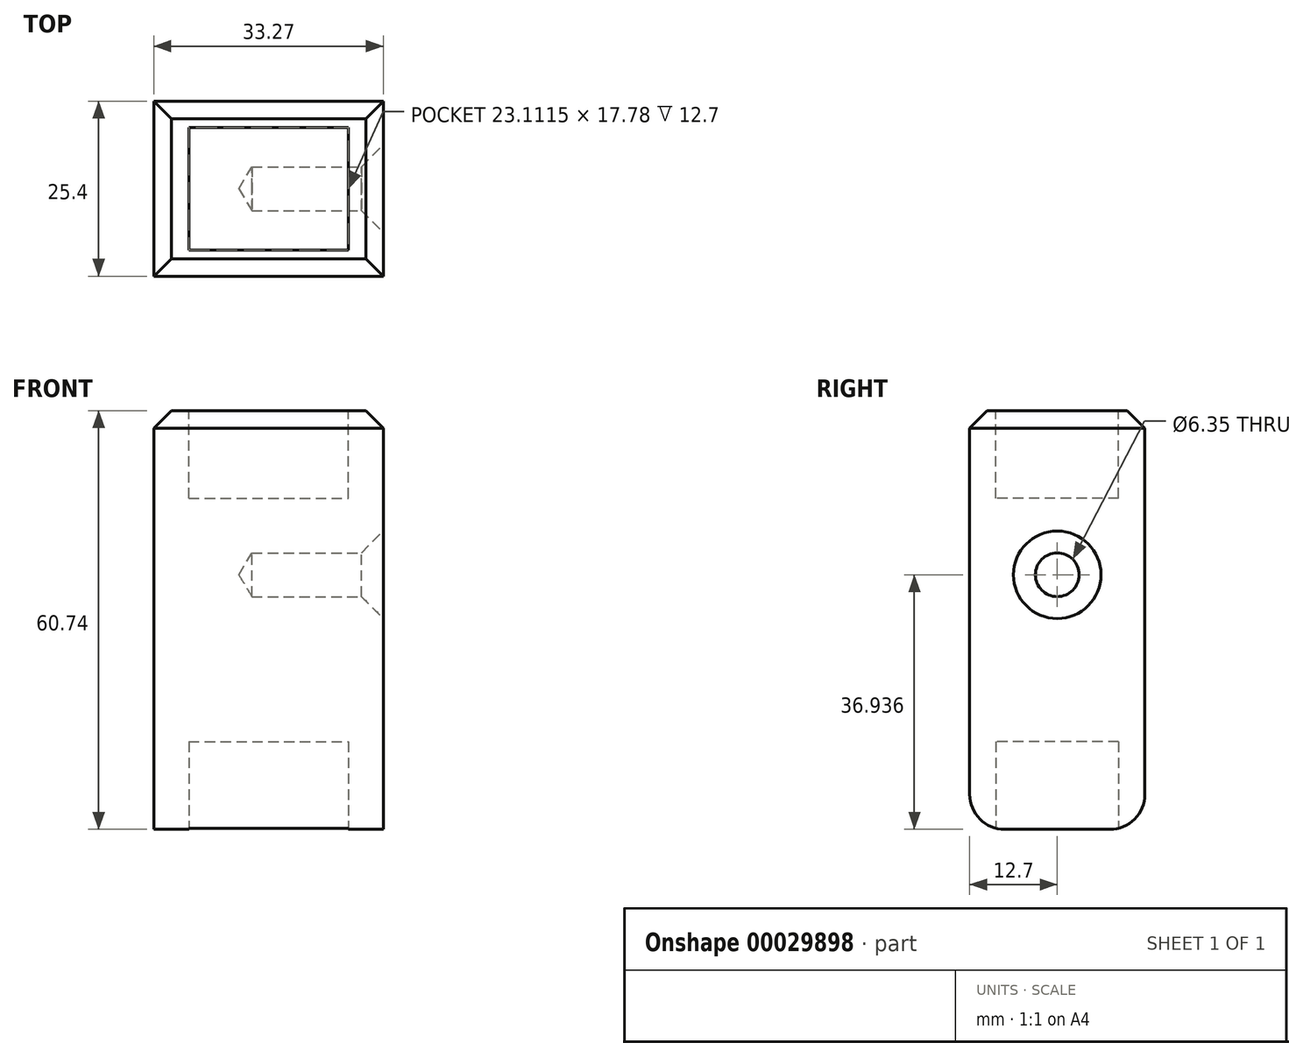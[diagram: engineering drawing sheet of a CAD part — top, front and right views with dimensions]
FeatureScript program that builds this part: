
annotation { "Feature Type Name" : "Feature", "Feature Type Description" : "" }
export const myFeature = defineFeature(function(context is Context, id is Id, definition is map)
    precondition{}
    {
        {
            var Q0;
            Q0=qCreatedBy(makeId("Front.planeOp"),FACE);
            var sketch = newSketch(context, id + "F0", { "sketchPlane" : qUnion([Q0])});
            skLineSegment(sketch, "E0", {"start": v(0, 0) * mm, "end": v(0, 30.37) * mm});
            skLineSegment(sketch, "E1", {"start": v(0, 30.37) * mm, "end": v(33.27, 30.37) * mm});
            skLineSegment(sketch, "E2", {"start": v(33.27, 30.37) * mm, "end": v(33.27, 0) * mm});
            skLineSegment(sketch, "E3", {"start": v(33.27, 0) * mm, "end": v(0, 0) * mm});
            skSolve(sketch);
        }
        {
            var Q0;
            Q0=makeQuery(id+"F0.imprint","IMPRINT",FACE,{"disambiguationData":[TD([[makeQuery(id+"F0.imprint","IMPRINT",EDGE,{"derivedFrom":sQuery(id+"F0.wireOp",EDGE,"E0")}),-1.0]])]});
            extrude(context, id + "F1", {"entities" : qUnion([Q0]), "depth" : 25.4 * mm});
        }
        {
            var Q0;
            Q0=makeQuery(id+"F1.opExtrude","SWEPT_FACE",FACE,{"disambiguationData":[OSD([sQuery(id+"F0.wireOp",EDGE,"E1")])]});
            var sketch = newSketch(context, id + "F2", { "sketchPlane" : qUnion([Q0])});
            skLineSegment(sketch, "E4.bottom", {"start": v(5.08, -3.81) * mm, "end": v(28.2, -3.81) * mm});
            skLineSegment(sketch, "E4.top", {"start": v(5.08, -21.59) * mm, "end": v(28.2, -21.59) * mm});
            skLineSegment(sketch, "E4.left", {"start": v(5.08, -3.81) * mm, "end": v(5.08, -21.59) * mm});
            skLineSegment(sketch, "E4.right", {"start": v(28.2, -3.81) * mm, "end": v(28.2, -21.59) * mm});
            skSolve(sketch);
        }
        {
            var Q0;
            Q0=makeQuery(id+"F2.imprint","IMPRINT",FACE,{"disambiguationData":[TD([[makeQuery(id+"F2.imprint","IMPRINT",EDGE,{"derivedFrom":sQuery(id+"F2.wireOp",EDGE,"E4.bottom")}),-1.0]])]});
            extrude(context, id + "F3", {"entities" : qUnion([Q0]), "operationType" : NewBodyOperationType.REMOVE, "oppositeDirection" : true, "depth" : 12.7 * mm});
        }
        {
            var Q0;
            Q0=makeQuery(id+"F1.opExtrude","SWEPT_BODY",BODY,{"disambiguationData":[OSD([sQuery(id+"F0.wireOp",EDGE,"E0"),sQuery(id+"F0.wireOp",EDGE,"E1"),sQuery(id+"F0.wireOp",EDGE,"E2"),sQuery(id+"F0.wireOp",EDGE,"E3")])]});
            var Q1;
            Q1=qCreatedBy(makeId("Top.planeOp"),FACE);
            mirror(context, id + "F4", {"operationType" : NewBodyOperationType.ADD, "entities" : qUnion([Q0]), "mirrorPlane" : qUnion([Q1])});
        }
        {
            var Q0;
            Q0=makeQuery(id+"F1.opExtrude","SWEPT_EDGE",EDGE,{"disambiguationData":[OSD([sQuery(id+"F0.wireOp",EDGE,"E0"),sQuery(id+"F0.wireOp",EDGE,"E1")])]});
            var Q1;
            Q1=makeQuery(id+"F1.opExtrude","CAP_EDGE",EDGE,{"disambiguationData":[OSD([sQuery(id+"F0.wireOp",EDGE,"E1")])],"isStart":false});
            var Q2;
            Q2=makeQuery(id+"F1.opExtrude","CAP_EDGE",EDGE,{"disambiguationData":[OSD([sQuery(id+"F0.wireOp",EDGE,"E1")])],"isStart":true});
            var Q3;
            Q3=makeQuery(id+"F1.opExtrude","SWEPT_EDGE",EDGE,{"disambiguationData":[OSD([sQuery(id+"F0.wireOp",EDGE,"E1"),sQuery(id+"F0.wireOp",EDGE,"E2")])]});
            chamfer(context, id + "F5", {"entities" : qUnion([Q0, Q1, Q2, Q3]), "width" : 2.54 * mm, "tangentPropagation" : true});
        }
        {
            var Q0;
            {var subQ0=makeQuery(id+"F1.opExtrude","CAP_FACE",FACE,{"disambiguationData":[OSD([sQuery(id+"F0.wireOp",EDGE,"E0"),sQuery(id+"F0.wireOp",EDGE,"E1"),sQuery(id+"F0.wireOp",EDGE,"E2"),sQuery(id+"F0.wireOp",EDGE,"E3")])],"isStart":false});Q0=makeQuery(id+"F4.boolean.opBoolean","MERGE",FACE,{"derivedFrom":[subQ0,makeQuery(id+"F4.opPattern","COPY",FACE,{"derivedFrom":subQ0,"instanceName":"1"})]});}
            var sketch = newSketch(context, id + "F6", { "sketchPlane" : qUnion([Q0])});
            skSolve(sketch);
        }
        {
            var Q0;
            {var subQ0=makeQuery(id+"F1.opExtrude","SWEPT_FACE",FACE,{"disambiguationData":[OSD([sQuery(id+"F0.wireOp",EDGE,"E2")])]});Q0=makeQuery(id+"F4.boolean.opBoolean","MERGE",FACE,{"derivedFrom":[subQ0,makeQuery(id+"F4.opPattern","COPY",FACE,{"derivedFrom":subQ0,"instanceName":"1"})]});}
            var sketch = newSketch(context, id + "F7", { "sketchPlane" : qUnion([Q0])});
            skCircle(sketch, "E5", {"center": v(-12.7, 6.57) * mm, "radius": 9.53 * mm});
            skSolve(sketch);
        }
        {
            var Q0;
            Q0=sQuery(id+"F7.wireOp",VERTEX,"E5.center");
            var Q1;
            Q1=makeQuery(id+"F1.opExtrude","SWEPT_BODY",BODY,{"disambiguationData":[OSD([sQuery(id+"F0.wireOp",EDGE,"E0"),sQuery(id+"F0.wireOp",EDGE,"E1"),sQuery(id+"F0.wireOp",EDGE,"E2"),sQuery(id+"F0.wireOp",EDGE,"E3")])]});
            hole(context, id + "F8", {"style" : HoleStyle.C_SINK, "holeDiameter" : 6.35 * mm, "cSinkDiameter" : 12.7 * mm, "endStyle" : HoleEndStyle.BLIND, "holeDepth" : 19.05 * mm, "locations" : qUnion([Q0]), "scope" : qUnion([Q1]), "cSinkAngle" : 90 * degree});
        }
        {
            var Q0;
            Q0=makeQuery(id+"F4.opPattern","COPY",EDGE,{"derivedFrom":makeQuery(id+"F1.opExtrude","CAP_EDGE",EDGE,{"disambiguationData":[OSD([sQuery(id+"F0.wireOp",EDGE,"E1")])],"isStart":true}),"instanceName":"1"});
            var Q1;
            Q1=makeQuery(id+"F4.opPattern","COPY",EDGE,{"derivedFrom":makeQuery(id+"F1.opExtrude","CAP_EDGE",EDGE,{"disambiguationData":[OSD([sQuery(id+"F0.wireOp",EDGE,"E1")])],"isStart":false}),"instanceName":"1"});
            fillet(context, id + "F9", {"entities" : qUnion([Q0, Q1]), "radius" : 5.08 * mm, "tangentPropagation" : true, "allowEdgeOverflow" : false});
        }
    });
